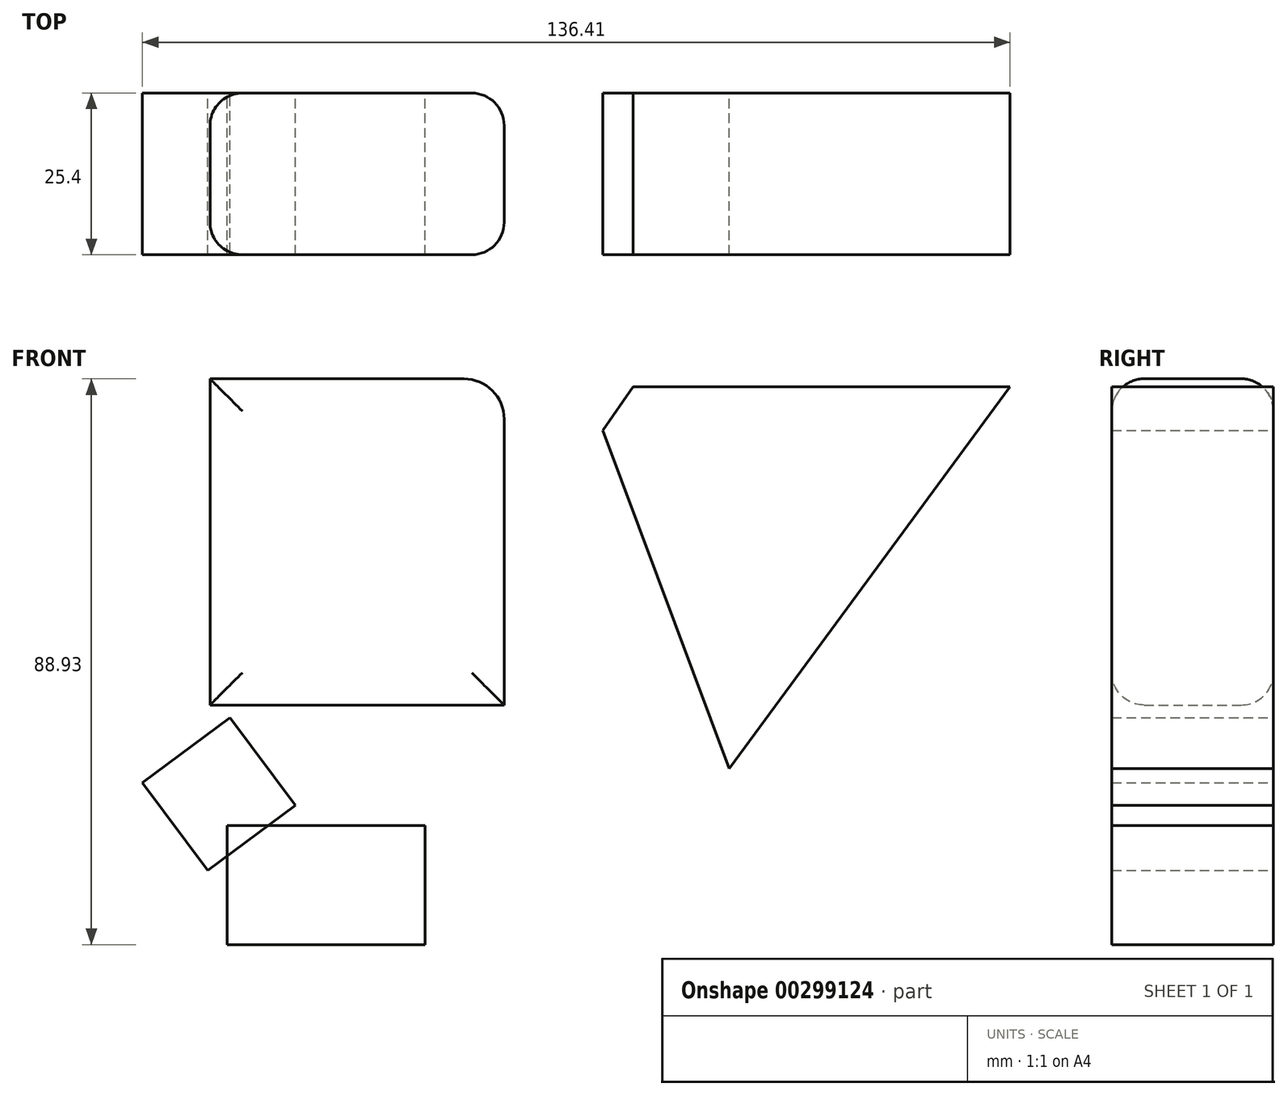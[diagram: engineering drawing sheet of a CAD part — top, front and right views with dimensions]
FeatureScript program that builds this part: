
annotation { "Feature Type Name" : "Feature", "Feature Type Description" : "" }
export const myFeature = defineFeature(function(context is Context, id is Id, definition is map)
    precondition{}
    {
        {
            var Q0;
            Q0=qCreatedBy(makeId("Front.planeOp"),FACE);
            var sketch = newSketch(context, id + "F0", { "sketchPlane" : qUnion([Q0])});
            skLineSegment(sketch, "E0.bottom", {"start": v(-10.2, -13.03) * mm, "end": v(-56.44, -13.03) * mm});
            skLineSegment(sketch, "E0.top", {"start": v(-16.56, 38.25) * mm, "end": v(-56.44, 38.25) * mm});
            skLineSegment(sketch, "E0.left", {"start": v(-10.2, -13.03) * mm, "end": v(-10.2, 31.9) * mm});
            skLineSegment(sketch, "E0.right", {"start": v(-56.44, -13.03) * mm, "end": v(-56.44, 38.25) * mm});
            skPoint(sketch, "E0.middle", {"position": v(-33.32, 12.6) * mm});
            skPoint(sketch, "E1.visualSharp", {"position": v(-10.2, 38.25) * mm});
            skArc(sketch, "E1.filletArc", {"start": v(-10.2, 31.9) * mm, "mid": v(-12.07, 36.39) * mm, "end": v(-16.56, 38.25) * mm});
            skLineSegment(sketch, "E2", {"start": v(2.77, 36.98) * mm, "end": v(69.34, 36.98) * mm});
            skLineSegment(sketch, "E3", {"start": v(69.34, 36.98) * mm, "end": v(25.15, -23.02) * mm});
            skLineSegment(sketch, "E4", {"start": v(25.15, -23.02) * mm, "end": v(2.77, 36.98) * mm});
            skCircle(sketch, "E5.cCircle", {"center": v(-55.05, -27.03) * mm, "radius": 8.59 * mm, "construction": true});
            skLineSegment(sketch, "E5.0", {"start": v(-43.04, -28.8) * mm, "end": v(-56.82, -39.04) * mm});
            skLineSegment(sketch, "E5.1", {"start": v(-56.82, -39.04) * mm, "end": v(-67.07, -25.26) * mm});
            skLineSegment(sketch, "E5.2", {"start": v(-67.07, -25.26) * mm, "end": v(-53.29, -15) * mm});
            skLineSegment(sketch, "E5.3", {"start": v(-53.29, -15) * mm, "end": v(-43.04, -28.8) * mm});
            skPoint(sketch, "E5.0.midPoint", {"position": v(-49.93, -33.92) * mm});
            skSolve(sketch);
        }
        {
            var Q0;
            Q0 = qSketchRegion(id + "F0", true);
            extrude(context, id + "F1", {"entities" : qUnion([Q0]), "depth" : 25.4 * mm});
        }
        {
            var Q0;
            Q0=qCreatedBy(makeId("Front.planeOp"),FACE);
            var sketch = newSketch(context, id + "F2", { "sketchPlane" : qUnion([Q0])});
            skLineSegment(sketch, "E6.bottom", {"start": v(-53.72, -31.94) * mm, "end": v(-22.61, -31.94) * mm});
            skLineSegment(sketch, "E6.top", {"start": v(-53.72, -50.68) * mm, "end": v(-22.61, -50.68) * mm});
            skLineSegment(sketch, "E6.left", {"start": v(-53.72, -31.94) * mm, "end": v(-53.72, -50.68) * mm});
            skLineSegment(sketch, "E6.right", {"start": v(-22.61, -31.94) * mm, "end": v(-22.61, -50.68) * mm});
            skSolve(sketch);
        }
        {
            var Q0;
            Q0=makeQuery(id+"F2.imprint","IMPRINT",FACE,{"disambiguationData":[TD([[makeQuery(id+"F2.imprint","IMPRINT",EDGE,{"derivedFrom":sQuery(id+"F2.wireOp",EDGE,"E6.bottom")}),-1.0]])]});
            extrude(context, id + "F3", {"entities" : qUnion([Q0]), "depth" : 25.4 * mm});
        }
        {
            var Q0;
            Q0=makeQuery(id+"F1.opExtrude","CAP_EDGE",EDGE,{"disambiguationData":[OSD([sQuery(id+"F0.wireOp",EDGE,"E0.bottom")])],"isStart":false});
            var Q1;
            Q1=makeQuery(id+"F1.opExtrude","CAP_EDGE",EDGE,{"disambiguationData":[OSD([sQuery(id+"F0.wireOp",EDGE,"E0.right")])],"isStart":false});
            var Q2;
            Q2=makeQuery(id+"F1.opExtrude","CAP_EDGE",EDGE,{"disambiguationData":[OSD([sQuery(id+"F0.wireOp",EDGE,"E0.left")])],"isStart":false});
            var Q3;
            Q3=makeQuery(id+"F1.opExtrude","CAP_EDGE",EDGE,{"disambiguationData":[OSD([sQuery(id+"F0.wireOp",EDGE,"E0.left")])],"isStart":true});
            var Q4;
            Q4=makeQuery(id+"F1.opExtrude","CAP_EDGE",EDGE,{"disambiguationData":[OSD([sQuery(id+"F0.wireOp",EDGE,"E0.bottom")])],"isStart":true});
            var Q5;
            Q5=makeQuery(id+"F1.opExtrude","CAP_EDGE",EDGE,{"disambiguationData":[OSD([sQuery(id+"F0.wireOp",EDGE,"E0.right")])],"isStart":true});
            fillet(context, id + "F4", {"entities" : qUnion([Q0, Q1, Q2, Q3, Q4, Q5]), "radius" : 5.08 * mm, "tangentPropagation" : true, "allowEdgeOverflow" : false});
        }
        {
            var Q0;
            Q0=makeQuery(id+"F1.opExtrude","SWEPT_EDGE",EDGE,{"disambiguationData":[OSD([sQuery(id+"F0.wireOp",EDGE,"E2"),sQuery(id+"F0.wireOp",EDGE,"E4")])]});
            chamfer(context, id + "F5", {"entities" : qUnion([Q0]), "width" : 5.08 * mm, "tangentPropagation" : true});
        }
    });
